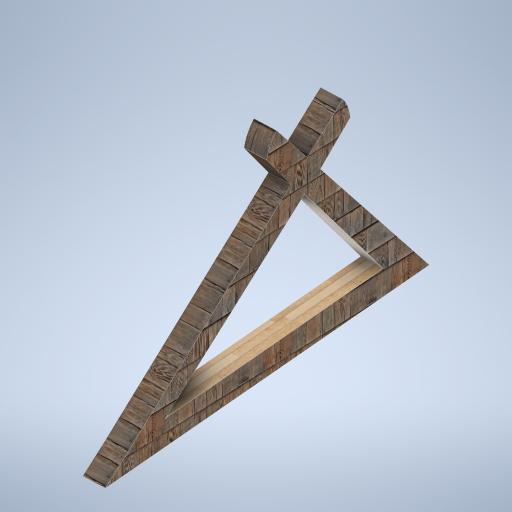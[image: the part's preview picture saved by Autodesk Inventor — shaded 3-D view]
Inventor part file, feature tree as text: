
AUTODESK INVENTOR PART (.ipt)
format: ipt  version: 2024.2 (Build 282272000, 272)  size: 460,800 bytes
history: native  units: mm
features: sketch x10, plane x6, extrude x4, projected_geometry x3, loft x2, other x1
ambient origin geometry x8: Origin, YZ Plane, XZ Plane, XY Plane, X Axis, Y Axis, Z Axis, Center Point
bodies: Solid1 (feature_tree)
feature tree (26):
  sketch  "Sketch1"  dims[d5=0.0mm d6=-8101.0mm d7=800.0mm]
  plane  "Work Plane2"
  loft  "Loft1"
  plane  "Work Plane3"
  extrude  "Extrusion1"  TaperAngle=0.0deg  [1 undecoded]
  sketch  "Sketch5"  dims[d15=6.981317mm d16=0.0mm d17=0.0mm]
  plane  "Work Plane4"
  extrude  "Extrusion2"  TaperAngle=0.0deg  [1 undecoded]
  plane  "Work Plane5"
  sketch  "Sketch7"  dims[d21=0.0mm d22=90.0deg d23=0.0mm d24=0.0mm]
  sketch  "Sketch8"  dims[d28=150.0mm d29=0.0mm]
  loft  "Loft2"
  sketch  "Sketch9"
  plane  "Work Plane6"
  extrude  "Extrusion3"  TaperAngle=0.0deg  [1 undecoded]
  extrude  "Extrusion4"  TaperAngle=0.0deg  [1 undecoded]
  plane  "Work Plane1"
  sketch  "Sketch2"  dims[d8=0.0mm d9=90.0deg d10=0.0mm d11=90.0deg]
  sketch  "Sketch3"  dims[d12=2600.0mm d13=0.0mm d14=0.0mm]
  sketch  "Sketch6"  dims[d18=90.0deg d19=0.0mm d20=90.0deg]
  projected_geometry  "Projected Loop1"
  projected_geometry  "Projected Loop2"
  other  "Edges1"
  projected_geometry  "Projected Loop3"
  sketch  "Sketch10"
  sketch  "Sketch11"
note: 4 required parameter values undecoded (feature->parameter linkage not recoverable at this tier; creation-order binding heuristic only, values carry confidence <= 0.55)
